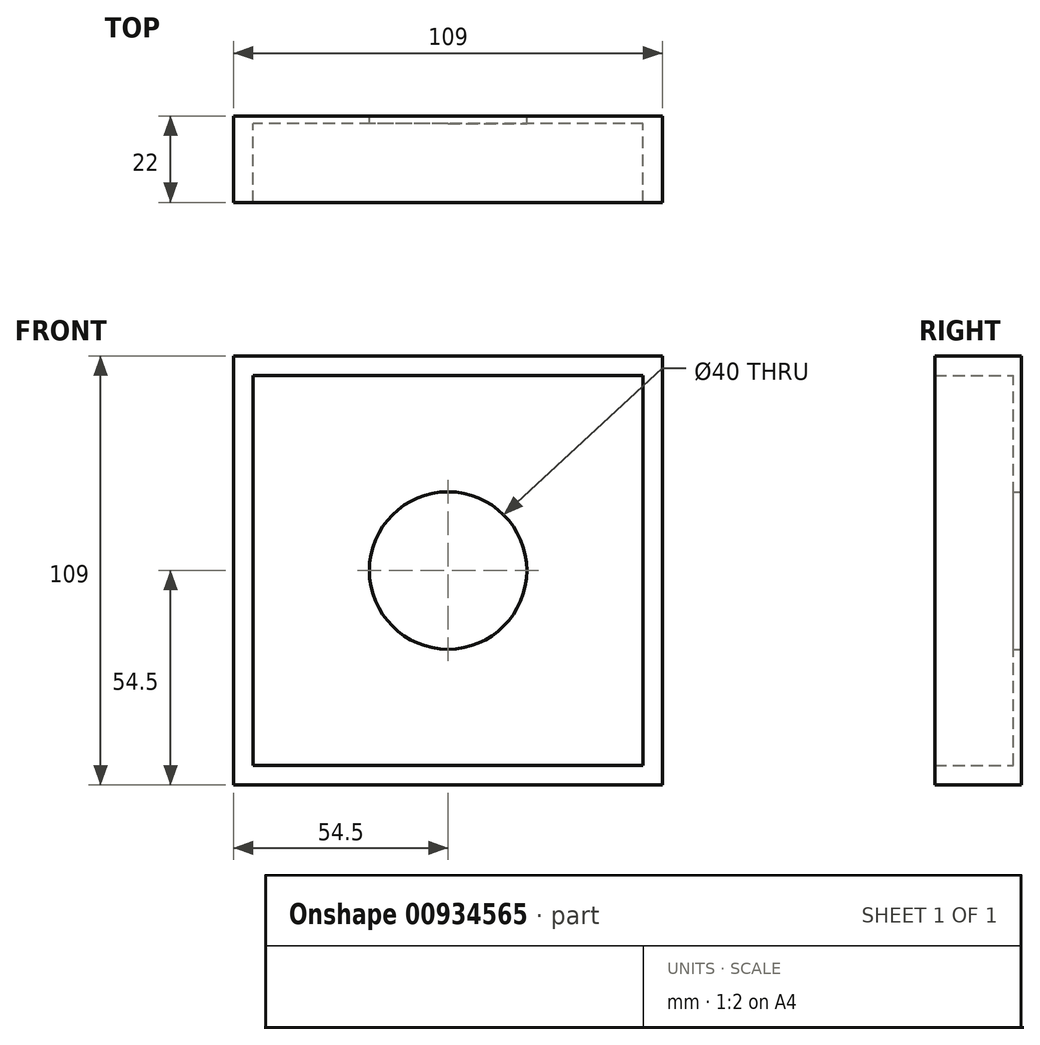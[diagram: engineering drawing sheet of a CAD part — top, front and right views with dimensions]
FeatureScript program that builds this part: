
annotation { "Feature Type Name" : "Feature", "Feature Type Description" : "" }
export const myFeature = defineFeature(function(context is Context, id is Id, definition is map)
    precondition{}
    {
        {
            assignVariable(context, id + "F0", {"name" : "faceSideWallWidth", "anyValue" : 5 * mm});
        }
        {
            assignVariable(context, id + "F1", {"name" : "wallWidth", "anyValue" : 2 * mm});
        }
        {
            assignVariable(context, id + "F2", {"name" : "cameraWidth", "anyValue" : 40 * mm});
        }
        {
            assignVariable(context, id + "F3", {"name" : "faceLip", "anyValue" : 20 * mm});
        }
        {
            var Q0;
            Q0=qCreatedBy(makeId("Front.planeOp"),FACE);
            var sketch = newSketch(context, id + "F4", { "sketchPlane" : qUnion([Q0])});
            skLineSegment(sketch, "E0.bottom", {"start": v(54.5, -54.5) * mm, "end": v(-54.5, -54.5) * mm});
            skLineSegment(sketch, "E0.top", {"start": v(54.5, 54.5) * mm, "end": v(-54.5, 54.5) * mm});
            skLineSegment(sketch, "E0.left", {"start": v(54.5, -54.5) * mm, "end": v(54.5, 54.5) * mm});
            skLineSegment(sketch, "E0.right", {"start": v(-54.5, -54.5) * mm, "end": v(-54.5, 54.5) * mm});
            skPoint(sketch, "E0.middle", {"position": v(0, 0) * mm});
            skSolve(sketch);
        }
        {
            var Q0;
            Q0=makeQuery(id+"F4.imprint","IMPRINT",FACE,{"disambiguationData":[TD([[makeQuery(id+"F4.imprint","IMPRINT",EDGE,{"derivedFrom":sQuery(id+"F4.wireOp",EDGE,"E0.bottom")}),-1.0]])]});
            extrude(context, id + "F5", {"entities" : qUnion([Q0]), "depth" : getVariable(context, 'faceLip') + getVariable(context, 'wallWidth'), "offsetDistance" : 25 * mm});
        }
        {
            var Q0;
            Q0=makeQuery(id+"F5.opExtrude","CAP_FACE",FACE,{"disambiguationData":[OSD([sQuery(id+"F4.wireOp",EDGE,"E0.bottom"),sQuery(id+"F4.wireOp",EDGE,"E0.top"),sQuery(id+"F4.wireOp",EDGE,"E0.left"),sQuery(id+"F4.wireOp",EDGE,"E0.right")])],"isStart":false});
            shell(context, id + "F6", {"entities" : qUnion([Q0]), "thickness" : getVariable(context, 'faceSideWallWidth')});
        }
        {
            var Q0;
            Q0=makeQuery(id+"F6.opShell","OFFSET_FACE",FACE,{"disambiguationData":[OSD([sQuery(id+"F4.wireOp",EDGE,"E0.bottom"),sQuery(id+"F4.wireOp",EDGE,"E0.top"),sQuery(id+"F4.wireOp",EDGE,"E0.left"),sQuery(id+"F4.wireOp",EDGE,"E0.right")])]});
            extrude(context, id + "F7", {"entities" : qUnion([Q0]), "operationType" : NewBodyOperationType.REMOVE, "oppositeDirection" : true, "depth" : getVariable(context, 'faceSideWallWidth') - getVariable(context, 'wallWidth'), "offsetDistance" : 25 * mm});
        }
        {
            var Q0;
            Q0=makeQuery(id+"F5.opExtrude","CAP_FACE",FACE,{"disambiguationData":[OSD([sQuery(id+"F4.wireOp",EDGE,"E0.bottom"),sQuery(id+"F4.wireOp",EDGE,"E0.top"),sQuery(id+"F4.wireOp",EDGE,"E0.left"),sQuery(id+"F4.wireOp",EDGE,"E0.right")])],"isStart":true});
            var sketch = newSketch(context, id + "F8", { "sketchPlane" : qUnion([Q0])});
            skPoint(sketch, "E1", {"position": v(0, 0) * mm});
            skSolve(sketch);
        }
        {
            var Q0;
            Q0=sQuery(id+"F8.wireOp",VERTEX,"E1");
            var Q1;
            Q1=makeQuery(id+"F5.opExtrude","SWEPT_BODY",BODY,{"disambiguationData":[OSD([sQuery(id+"F4.wireOp",EDGE,"E0.bottom"),sQuery(id+"F4.wireOp",EDGE,"E0.top"),sQuery(id+"F4.wireOp",EDGE,"E0.left"),sQuery(id+"F4.wireOp",EDGE,"E0.right")])]});
            hole(context, id + "F9", {"style" : HoleStyle.SIMPLE, "endStyle" : HoleEndStyle.THROUGH, "holeDiameter" : getVariable(context, 'cameraWidth'), "majorDiameter" : 5 * mm, "isTappedThrough" : true, "tappedDepth" : 12 * mm, "tapClearance" : 3, "locations" : qUnion([Q0]), "scope" : qUnion([Q1])});
        }
    });
